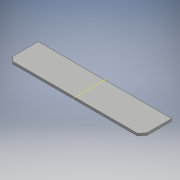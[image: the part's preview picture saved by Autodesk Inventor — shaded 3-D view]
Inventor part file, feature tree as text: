
AUTODESK INVENTOR PART (.ipt)
format: ipt  version: 2018 (Build 220112000, 112)  size: 123,904 bytes
history: native  units: mm
features: other x5, plane x1, sheet_metal_op x1, sketch x1, reference x1
ambient origin geometry x8: Origin, YZ Plane, XZ Plane, XY Plane, X Axis, Y Axis, Z Axis, Center Point
bodies: Solid1 (feature_tree)
feature tree (9):
  plane  "Work Plane1"
  sheet_metal_op  "Face1"
  other  "midtplan"
  sketch  "Sketch1"  dims[d3=45.0deg d4=7.171149mm d5=30.0mm d6=2.0mm d7=2.0mm]
  reference  "Reference1"
  other  "Plate1"
  parser-record x1  (decoder bookkeeping rows leaked as tree rows — omitted from the tree; the rows remain in map.json)
  other  "modul.iam"
  other  "plade:1"
note: 1 file-system path scrubbed to <path> (originals preserved in map.json)
